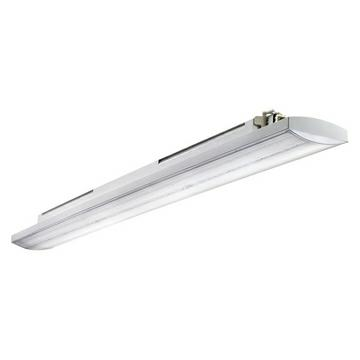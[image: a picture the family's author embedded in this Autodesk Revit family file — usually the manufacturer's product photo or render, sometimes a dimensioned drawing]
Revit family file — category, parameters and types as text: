
# Revit family: Lighting-Industriale-GEWISS-SMART[3]PLUS-PLAFONIERA-LED_TRANSPARENTE_1600mm
name_source: partatom
category: Apparecchi per illuminazione
units: mm (PartAtom-declared; Revit-internal decimal feet)

## family parameters
Condiviso = No
Host = Superficie
Punto di calcolo locali = No
Quota connettore circolare = Usa diametro
Sorgente d'illuminazione = Sì
Taglio con vuoti quando caricato = No
Tipo di parte = Normale

## types (1)
- Lighting-Industriale-GEWISS-SMART[3]PLUS-PLAFONIERA-LED_TRANSPARENTE_1600mm
    Angolo inclinazione = -90.00°
    Applicazione = Interno
    Carico apparente = 67 VA
    Catalogo = LIGHTING
    Catalogo Serie = SMART[3] PLUS
    Classe di efficienza LED integrati = A ÷ A++
    Classe isolamento = II
    Codice Electrocod = 2434
    Commenti sul wattaggio = 67W
    Descrizione = SMART3 PLUS 1600 T.W.DALI HE TRASP 9 57
    Emetti da lunghezza linea = 1200 mm
    File diagramma fotometrico = GWS3323AT957.IES
    Filtro dei colori = 16777215
    Ganci = Alluminio
    Garanzia = 5 anni
    Glow Wire Test = 850°C
    Grado di protezione = IP66/IP69
    IDF = be41a214-2304-4719-b36b-5e7545f50e73
    IDT = 5236158c-1d15-421c-8690-1b1aa3a85baf
    Immagine tipo = GWS3280TS.jpg
    Lampada = LED
    Lampada: = LED
    Lumen output (lm) = 5900
    Lunghezza = 1600 mm
    Lunghezza Lampada = 1600 mm  [stored 5.24934 ft]
    Modello = GWS3323AT957
    Numero poli = 2
    Potenza di sistema = 50 W
    Produttore = GEWISS S.p.A.
    Prospetto di default = 1219 mm
    Resistenza agli urti = IK08
    SEO = Plafoniera
    Scheda Tecnica = https://www.gewiss.com
    Schermo = Trasparente
    Schermo. = Led Acceso
    Stampa 1_100 = Sì
    Stampa 1_200 = No
    Struttura = GRIGIO
    Temperatura di colore = 5700 K (CRI > 90)
    Temperatura di colore: = 5700 K (CRI > 90)
    Temperatura di funzionamento = -25 +50 °C
    Temperatura di utilizzo = -25 +50 °C
    Tensione = 220-240 V
    Tipologia = DALI
    Tipologia sorgente luminosa = LED - Non sostituibile
    URL = https://www.gewiss.com
    Variazione temperatura colore lampada con luminosità attenuata = <Nessuno>
    Versione file RFA = 20.0

note: [stored X ft] marks values corroborated as IEEE doubles in the binary element streams (Revit-internal decimal feet)
